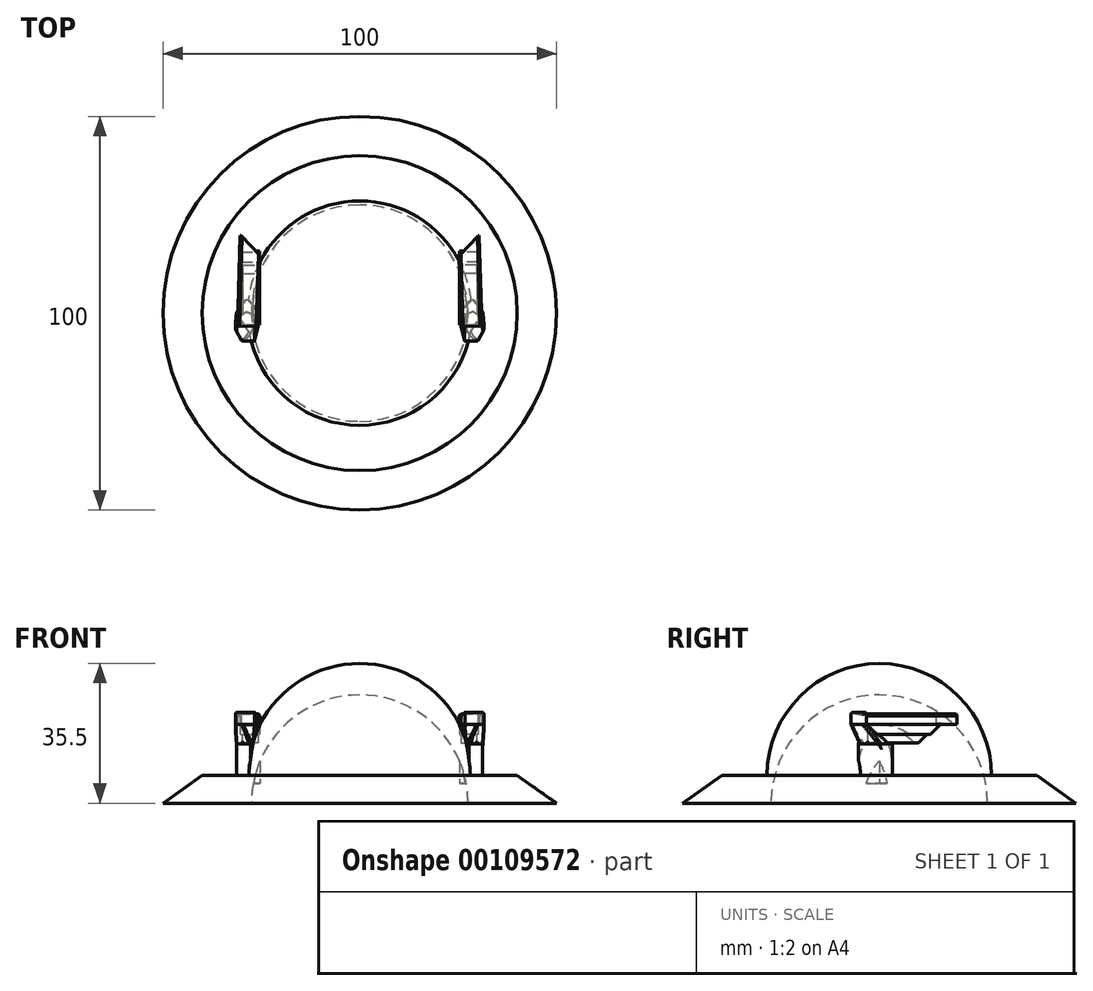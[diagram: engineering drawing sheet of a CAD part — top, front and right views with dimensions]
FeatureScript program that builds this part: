
annotation { "Feature Type Name" : "Feature", "Feature Type Description" : "" }
export const myFeature = defineFeature(function(context is Context, id is Id, definition is map)
    precondition{}
    {
        {
            var Q0;
            Q0=qCreatedBy(makeId("Top.planeOp"),FACE);
            var sketch = newSketch(context, id + "F0", { "sketchPlane" : qUnion([Q0])});
            skArc(sketch, "E0", {"start": v(0, 50) * mm, "mid": v(-50, 0) * mm, "end": v(0, -50) * mm});
            skLineSegment(sketch, "E1", {"start": v(0, 50) * mm, "end": v(0, -50) * mm});
            skSolve(sketch);
        }
        {
            var Q0;
            Q0=qCreatedBy(makeId("Top.planeOp"),FACE);
            cPlane(context, id + "F1", {"entities" : qUnion([Q0]), "cplaneType" : CPlaneType.OFFSET, "offset" : 7 * mm, "width" : 150 * mm, "height" : 150 * mm});
        }
        {
            var Q0;
            Q0=qCreatedBy(id+"F1.planeOp",FACE);
            var sketch = newSketch(context, id + "F2", { "sketchPlane" : qUnion([Q0])});
            skArc(sketch, "E2", {"start": v(0, 40) * mm, "mid": v(-40, 0) * mm, "end": v(0, -40) * mm});
            skLineSegment(sketch, "E3", {"start": v(0, 40) * mm, "end": v(0, -40) * mm});
            skSolve(sketch);
        }
        {
            var Q0;
            Q0=makeQuery(id+"F0.imprint","IMPRINT",FACE,{"disambiguationData":[TD([[makeQuery(id+"F0.imprint","IMPRINT",EDGE,{"derivedFrom":sQuery(id+"F0.wireOp",EDGE,"E0")}),1.0]])]});
            var Q1;
            Q1=makeQuery(id+"F2.imprint","IMPRINT",FACE,{"disambiguationData":[TD([[makeQuery(id+"F2.imprint","IMPRINT",EDGE,{"derivedFrom":sQuery(id+"F2.wireOp",EDGE,"E2")}),1.0]])]});
            loft(context, id + "F3", {"sheetProfilesArray" : [{ "sheetProfileEntities" : qUnion([Q0]) }, { "sheetProfileEntities" : qUnion([Q1]) }]});
        }
        {
            var Q0;
            Q0=makeQuery(id+"F3.opLoft","CAP_FACE",FACE,{"disambiguationData":[OSD([makeQuery(id+"F2.imprint","IMPRINT",FACE,{"disambiguationData":[TD([[makeQuery(id+"F2.imprint","IMPRINT",EDGE,{"derivedFrom":sQuery(id+"F2.wireOp",EDGE,"E2")}),1.0]])]})])],"isStart":true});
            var sketch = newSketch(context, id + "F4", { "sketchPlane" : qUnion([Q0])});
            skArc(sketch, "E4", {"start": v(0, 28.5) * mm, "mid": v(-28.5, 0) * mm, "end": v(0, -28.5) * mm});
            skLineSegment(sketch, "E5", {"start": v(0, 28.5) * mm, "end": v(0, -28.5) * mm});
            skSolve(sketch);
        }
        {
            var Q0;
            Q0 = qSketchRegion(id + "F4", true);
            var Q1;
            Q1=sQuery(id+"F4.wireOp",EDGE,"E5");
            revolve(context, id + "F5", {"operationType" : NewBodyOperationType.ADD, "entities" : qUnion([Q0]), "axis" : qUnion([Q1]), "revolveType" : RevolveType.ONE_DIRECTION, "oppositeDirection" : true, "angle" : 90 * degree});
        }
        {
            var Q0;
            Q0=makeQuery(id+"F3.opLoft","CAP_FACE",FACE,{"disambiguationData":[OSD([makeQuery(id+"F0.imprint","IMPRINT",FACE,{"disambiguationData":[TD([[makeQuery(id+"F0.imprint","IMPRINT",EDGE,{"derivedFrom":sQuery(id+"F0.wireOp",EDGE,"E0")}),1.0]])]})])],"isStart":true});
            var sketch = newSketch(context, id + "F6", { "sketchPlane" : qUnion([Q0])});
            skArc(sketch, "E6", {"start": v(0, 27.5) * mm, "mid": v(-27.5, 0) * mm, "end": v(0, -27.5) * mm});
            skLineSegment(sketch, "E7", {"start": v(0, 27.5) * mm, "end": v(0, -27.5) * mm});
            skSolve(sketch);
        }
        {
            var Q0;
            Q0 = qSketchRegion(id + "F6", true);
            var Q1;
            Q1=sQuery(id+"F6.wireOp",EDGE,"E7");
            revolve(context, id + "F7", {"operationType" : NewBodyOperationType.REMOVE, "entities" : qUnion([Q0]), "axis" : qUnion([Q1]), "revolveType" : RevolveType.FULL, "oppositeDirection" : true});
        }
        {
            var Q0;
            Q0=qCreatedBy(makeId("Top.planeOp"),FACE);
            cPlane(context, id + "F8", {"entities" : qUnion([Q0]), "cplaneType" : CPlaneType.OFFSET, "offset" : 5 * mm, "width" : 150 * mm, "height" : 150 * mm});
        }
        {
            var Q0;
            Q0=qCreatedBy(id+"F8.planeOp",FACE);
            var sketch = newSketch(context, id + "F9", { "sketchPlane" : qUnion([Q0])});
            skLineSegment(sketch, "E8", {"start": v(-31.44, 0) * mm, "end": v(-27.73, -5.29) * mm});
            skLineSegment(sketch, "E9", {"start": v(-27.73, -5.29) * mm, "end": v(-25.32, 0) * mm});
            skLineSegment(sketch, "E10", {"start": v(-25.32, 0) * mm, "end": v(-28.66, 3.99) * mm});
            skLineSegment(sketch, "E11", {"start": v(-28.66, 3.99) * mm, "end": v(-31.44, 0) * mm});
            skSolve(sketch);
        }
        {
            var Q0;
            Q0 = qSketchRegion(id + "F9", true);
            extrude(context, id + "F10", {"entities" : qUnion([Q0]), "operationType" : NewBodyOperationType.ADD, "depth" : 10 * mm});
        }
        {
            var Q0;
            Q0=qCreatedBy(makeId("Top.planeOp"),FACE);
            cPlane(context, id + "F11", {"entities" : qUnion([Q0]), "cplaneType" : CPlaneType.OFFSET, "offset" : 20 * mm, "width" : 150 * mm, "height" : 150 * mm});
        }
        {
            var Q0;
            Q0=qCreatedBy(id+"F11.planeOp",FACE);
            var sketch = newSketch(context, id + "F12", { "sketchPlane" : qUnion([Q0])});
            skLineSegment(sketch, "E12", {"start": v(-29.87, -7.14) * mm, "end": v(-32.1, -3.25) * mm});
            skLineSegment(sketch, "E13", {"start": v(-32.1, -3.25) * mm, "end": v(-25.79, -3.43) * mm});
            skLineSegment(sketch, "E14", {"start": v(-25.79, -3.43) * mm, "end": v(-26.71, -7.14) * mm});
            skLineSegment(sketch, "E15", {"start": v(-26.71, -7.14) * mm, "end": v(-29.87, -7.14) * mm});
            skSolve(sketch);
        }
        {
            var Q1;
            Q1 = qSketchRegion(id + "F12", true);
            var Q2;
            Q2=makeQuery(id+"F10.opExtrude","CAP_FACE",FACE,{"disambiguationData":[OSD([sQuery(id+"F9.wireOp",EDGE,"E8"),sQuery(id+"F9.wireOp",EDGE,"E9"),sQuery(id+"F9.wireOp",EDGE,"E10"),sQuery(id+"F9.wireOp",EDGE,"E11")])],"isStart":false});
            loft(context, id + "F13", {"operationType" : NewBodyOperationType.ADD, "sheetProfilesArray" : [{ "sheetProfileEntities" : qUnion([Q1]) }, { "sheetProfileEntities" : qUnion([Q2]) }]});
        }
        {
            var Q0;
            Q0=makeQuery(id+"F10.opExtrude","SWEPT_EDGE",EDGE,{"disambiguationData":[OSD([sQuery(id+"F9.wireOp",EDGE,"E8"),sQuery(id+"F9.wireOp",EDGE,"E11")])]});
            var Q1;
            Q1=makeQuery(id+"F10.opExtrude","SWEPT_EDGE",EDGE,{"disambiguationData":[OSD([sQuery(id+"F9.wireOp",EDGE,"E10"),sQuery(id+"F9.wireOp",EDGE,"E11")])]});
            fillet(context, id + "F14", {"entities" : qUnion([Q0, Q1]), "radius" : 1 * mm, "tangentPropagation" : true, "allowEdgeOverflow" : false});
        }
        {
            var Q0;
            Q0=makeQuery(id+"F13.opLoft","SWEPT_EDGE",EDGE,{"disambiguationData":[OSD([sQuery(id+"F9.wireOp",EDGE,"E8"),sQuery(id+"F9.wireOp",EDGE,"E9"),sQuery(id+"F9.wireOp",EDGE,"E11"),sQuery(id+"F12.wireOp",EDGE,"E12")])]});
            var Q1;
            Q1=makeQuery(id+"F13.opLoft","SWEPT_EDGE",EDGE,{"disambiguationData":[OSD([sQuery(id+"F9.wireOp",EDGE,"E10"),sQuery(id+"F9.wireOp",EDGE,"E11"),sQuery(id+"F12.wireOp",EDGE,"E12"),sQuery(id+"F12.wireOp",EDGE,"E13")])]});
            fillet(context, id + "F15", {"entities" : qUnion([Q0, Q1]), "radius" : 0.5 * mm, "tangentPropagation" : true, "allowEdgeOverflow" : false});
        }
        {
            var Q0;
            Q0=makeQuery(id+"F13.opLoft","CAP_FACE",FACE,{"disambiguationData":[OSD([makeQuery(id+"F12.imprint","IMPRINT",FACE,{"disambiguationData":[TD([[makeQuery(id+"F12.imprint","IMPRINT",EDGE,{"derivedFrom":sQuery(id+"F12.wireOp",EDGE,"E12")}),-1.0]])]})])],"isStart":true});
            extrude(context, id + "F16", {"entities" : qUnion([Q0]), "operationType" : NewBodyOperationType.ADD, "depth" : 3 * mm});
        }
        {
            var Q0;
            Q0=makeQuery(id+"F16.opExtrude","CAP_EDGE",EDGE,{"disambiguationData":[OSD([sQuery(id+"F9.wireOp",EDGE,"E8"),sQuery(id+"F9.wireOp",EDGE,"E9"),sQuery(id+"F12.wireOp",EDGE,"E12"),sQuery(id+"F12.wireOp",EDGE,"E13"),sQuery(id+"F12.wireOp",EDGE,"E15")])],"isStart":false});
            var Q1;
            Q1=makeQuery(id+"F16.opExtrude","CAP_EDGE",EDGE,{"disambiguationData":[OSD([sQuery(id+"F12.wireOp",EDGE,"E12"),sQuery(id+"F12.wireOp",EDGE,"E14"),sQuery(id+"F12.wireOp",EDGE,"E15")])],"isStart":false});
            var Q2;
            Q2=makeQuery(id+"F16.opExtrude","SWEPT_EDGE",EDGE,{"disambiguationData":[OSD([sQuery(id+"F12.wireOp",EDGE,"E12"),sQuery(id+"F12.wireOp",EDGE,"E15")])]});
            var Q3;
            {var subQ0=sQuery(id+"F12.wireOp",EDGE,"E12");var subQ1=sQuery(id+"F12.wireOp",EDGE,"E13");Q3=makeQuery(id+"F16.opExtrude","SWEPT_EDGE",EDGE,{"disambiguationData":[OSD([sQuery(id+"F9.wireOp",EDGE,"E8"),sQuery(id+"F9.wireOp",EDGE,"E9"),sQuery(id+"F9.wireOp",EDGE,"E10"),sQuery(id+"F9.wireOp",EDGE,"E11"),subQ0,subQ1,makeQuery(id+"F12.imprint","IMPRINT",FACE,{"disambiguationData":[TD([[makeQuery(id+"F12.imprint","IMPRINT",EDGE,{"derivedFrom":subQ0}),-1.0]])]})])]});}
            fillet(context, id + "F17", {"entities" : qUnion([Q0, Q1, Q2, Q3]), "radius" : 0.3 * mm, "tangentPropagation" : true, "allowEdgeOverflow" : false});
        }
        {
            var Q0;
            Q0=makeQuery(id+"F16.opExtrude","SWEPT_FACE",FACE,{"disambiguationData":[OSD([sQuery(id+"F12.wireOp",EDGE,"E12"),sQuery(id+"F12.wireOp",EDGE,"E13"),sQuery(id+"F12.wireOp",EDGE,"E14")])]});
            extrude(context, id + "F18", {"entities" : qUnion([Q0]), "operationType" : NewBodyOperationType.ADD, "depth" : 23 * mm});
        }
        {
            var Q0;
            {var subQ0=sQuery(id+"F12.wireOp",EDGE,"E14");var subQ1=sQuery(id+"F12.wireOp",EDGE,"E13");var subQ2=sQuery(id+"F12.wireOp",EDGE,"E12");Q0=makeQuery(id+"F18.opExtrude","CAP_EDGE",EDGE,{"disambiguationData":[OSD([subQ2,subQ1,subQ0]),TDD([makeQuery(id+"F16.boolean.opBoolean","MERGE",EDGE,{"derivedFrom":[makeQuery(id+"F13.opLoft","MID_CAP_EDGE",EDGE,{"disambiguationData":[OSD([subQ2,subQ1,subQ0])],"capPos":0.0}),makeQuery(id+"F16.opExtrude","CAP_EDGE",EDGE,{"disambiguationData":[OSD([subQ2,subQ1,subQ0])],"isStart":true})]})])],"isStart":false});}
            chamfer(context, id + "F19", {"entities" : qUnion([Q0]), "width" : 5 * mm, "tangentPropagation" : true});
        }
        {
            var Q0;
            {var subQ0=sQuery(id+"F12.wireOp",EDGE,"E12");var subQ1=sQuery(id+"F12.wireOp",EDGE,"E13");var subQ2=sQuery(id+"F12.wireOp",EDGE,"E14");var subQ3=sQuery(id+"F12.wireOp",EDGE,"E15");Q0=makeQuery(id+"F18.opExtrude","SWEPT_EDGE",EDGE,{"disambiguationData":[OSD([sQuery(id+"F9.wireOp",EDGE,"E8"),sQuery(id+"F9.wireOp",EDGE,"E9"),sQuery(id+"F9.wireOp",EDGE,"E10"),sQuery(id+"F9.wireOp",EDGE,"E11"),subQ0,subQ1,subQ2,subQ3,makeQuery(id+"F12.imprint","IMPRINT",FACE,{"disambiguationData":[TD([[makeQuery(id+"F12.imprint","IMPRINT",EDGE,{"derivedFrom":subQ0}),-1.0]])]})])]});}
            var Q1;
            Q1=makeQuery(id+"F18.opExtrude","SWEPT_EDGE",EDGE,{"disambiguationData":[OSD([sQuery(id+"F12.wireOp",EDGE,"E12"),sQuery(id+"F12.wireOp",EDGE,"E13"),sQuery(id+"F12.wireOp",EDGE,"E14"),sQuery(id+"F12.wireOp",EDGE,"E15")])]});
            chamfer(context, id + "F20", {"entities" : qUnion([Q0, Q1]), "width" : 0.5 * mm, "tangentPropagation" : true});
        }
        {
            var Q0;
            Q0=qCreatedBy(makeId("Front.planeOp"),FACE);
            cPlane(context, id + "F21", {"entities" : qUnion([Q0]), "cplaneType" : CPlaneType.OFFSET, "offset" : 3 * mm, "width" : 150 * mm, "height" : 150 * mm});
        }
        {
            var Q0;
            Q0=qCreatedBy(id+"F21.planeOp",FACE);
            var sketch = newSketch(context, id + "F22", { "sketchPlane" : qUnion([Q0])});
            skLineSegment(sketch, "E16.bottom", {"start": v(-25.4, 20.22) * mm, "end": v(-30.24, 20.22) * mm});
            skLineSegment(sketch, "E16.top", {"start": v(-25.4, 17.5) * mm, "end": v(-30.24, 17.5) * mm});
            skLineSegment(sketch, "E16.left", {"start": v(-25.4, 20.22) * mm, "end": v(-25.4, 17.5) * mm});
            skLineSegment(sketch, "E16.right", {"start": v(-30.24, 20.22) * mm, "end": v(-30.24, 17.5) * mm});
            skSolve(sketch);
        }
        {
            var Q0;
            Q0 = qSketchRegion(id + "F22", true);
            extrude(context, id + "F23", {"entities" : qUnion([Q0]), "operationType" : NewBodyOperationType.ADD, "oppositeDirection" : true, "depth" : 19 * mm});
        }
        {
            var Q0;
            Q0=makeQuery(id+"F23.opExtrude","CAP_EDGE",EDGE,{"disambiguationData":[OSD([sQuery(id+"F22.wireOp",EDGE,"E16.top")])],"isStart":false});
            chamfer(context, id + "F24", {"entities" : qUnion([Q0]), "width" : 3 * mm, "tangentPropagation" : true});
        }
        {
            var Q0;
            Q0=qCreatedBy(id+"F21.planeOp",FACE);
            var sketch = newSketch(context, id + "F25", { "sketchPlane" : qUnion([Q0])});
            skLineSegment(sketch, "E17.bottom", {"start": v(-25.76, 17.45) * mm, "end": v(-29.75, 17.45) * mm});
            skLineSegment(sketch, "E17.top", {"start": v(-25.76, 15.29) * mm, "end": v(-29.75, 15.29) * mm});
            skLineSegment(sketch, "E17.left", {"start": v(-25.76, 17.45) * mm, "end": v(-25.76, 15.29) * mm});
            skLineSegment(sketch, "E17.right", {"start": v(-29.75, 17.45) * mm, "end": v(-29.75, 15.29) * mm});
            skSolve(sketch);
        }
        {
            var Q0;
            Q0 = qSketchRegion(id + "F25", true);
            extrude(context, id + "F26", {"entities" : qUnion([Q0]), "operationType" : NewBodyOperationType.ADD, "oppositeDirection" : true, "depth" : 18 * mm});
        }
        {
            var Q0;
            Q0=makeQuery(id+"F26.opExtrude","CAP_EDGE",EDGE,{"disambiguationData":[OSD([sQuery(id+"F25.wireOp",EDGE,"E17.top")])],"isStart":false});
            chamfer(context, id + "F27", {"entities" : qUnion([Q0]), "width" : 5 * mm, "tangentPropagation" : true});
        }
        {
            var Q0;
            Q0=makeQuery(id+"F3.opLoft","SWEPT_BODY",BODY,{"disambiguationData":[OSD([makeQuery(id+"F0.imprint","IMPRINT",FACE,{"disambiguationData":[TD([[makeQuery(id+"F0.imprint","IMPRINT",EDGE,{"derivedFrom":sQuery(id+"F0.wireOp",EDGE,"E0")}),1.0]])]}),makeQuery(id+"F2.imprint","IMPRINT",FACE,{"disambiguationData":[TD([[makeQuery(id+"F2.imprint","IMPRINT",EDGE,{"derivedFrom":sQuery(id+"F2.wireOp",EDGE,"E2")}),1.0]])]})])]});
            var Q1;
            Q1=qCreatedBy(makeId("Right.planeOp"),FACE);
            mirror(context, id + "F28", {"operationType" : NewBodyOperationType.ADD, "entities" : qUnion([Q0]), "mirrorPlane" : qUnion([Q1])});
        }
    });
